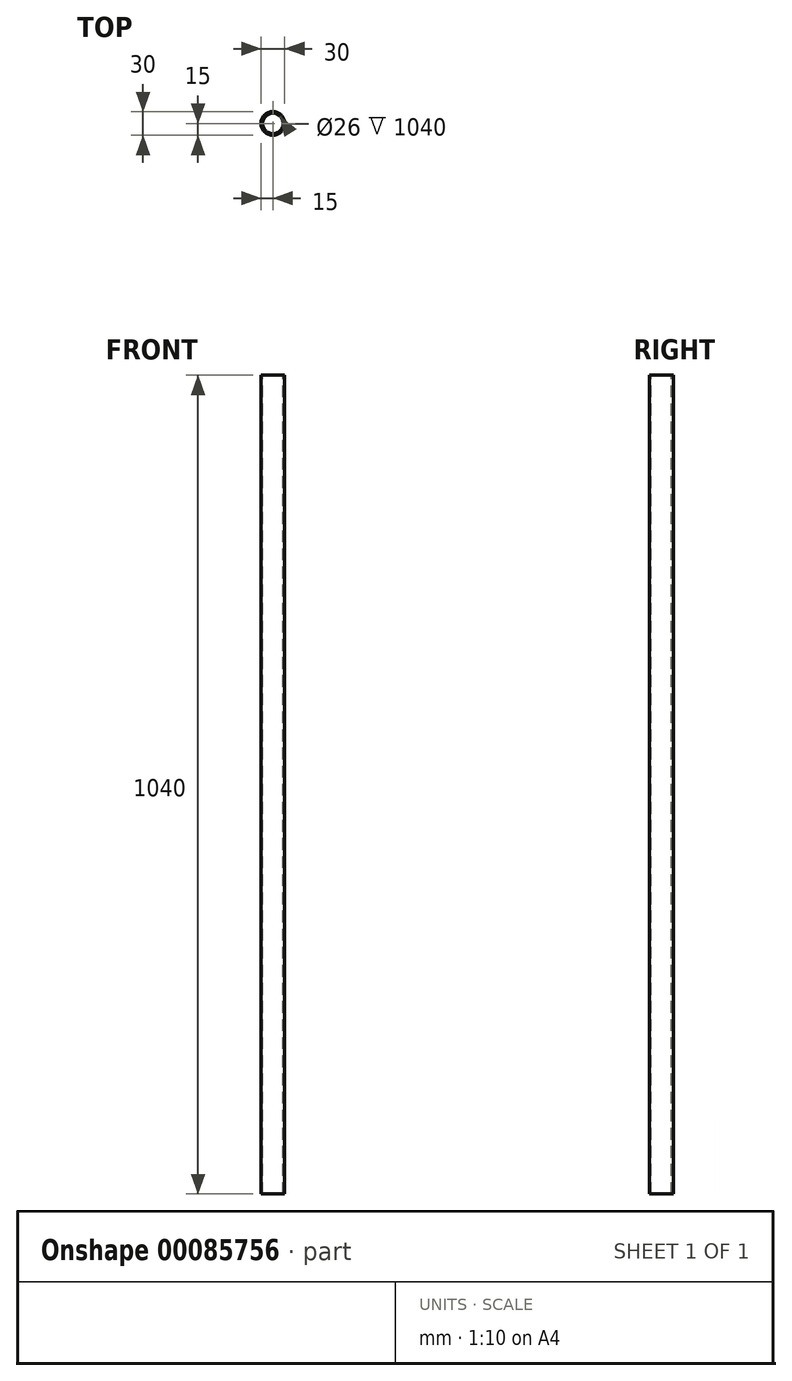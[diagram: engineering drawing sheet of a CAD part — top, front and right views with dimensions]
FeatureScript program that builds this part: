
annotation { "Feature Type Name" : "Feature", "Feature Type Description" : "" }
export const myFeature = defineFeature(function(context is Context, id is Id, definition is map)
    precondition{}
    {
        {
            var Q0;
            Q0=qCreatedBy(makeId("Top.planeOp"),FACE);
            var sketch = newSketch(context, id + "F0", { "sketchPlane" : qUnion([Q0])});
            skCircle(sketch, "E0", {"center": v(0, 0) * mm, "radius": 15 * mm});
            skCircle(sketch, "E1", {"center": v(0, 0) * mm, "radius": 13 * mm});
            skSolve(sketch);
        }
        {
            var Q0;
            Q0 = qSketchRegion(id + "F0", true);
            extrude(context, id + "F1", {"entities" : qUnion([Q0]), "endBound" : BoundingType.SYMMETRIC, "oppositeDirection" : true, "depth" : 1040 * mm});
        }
    });
